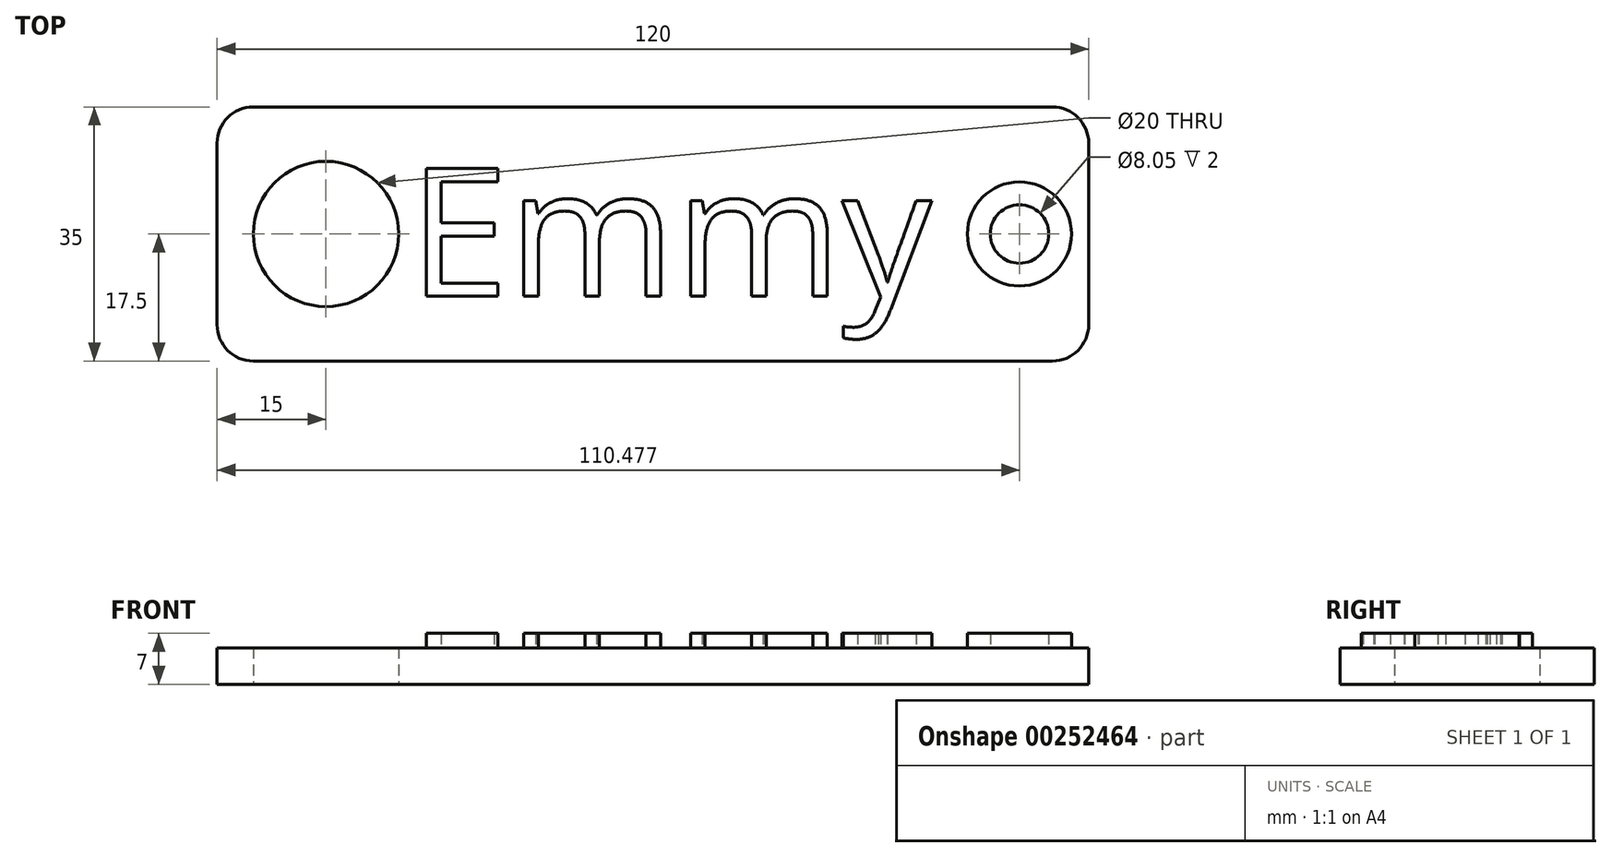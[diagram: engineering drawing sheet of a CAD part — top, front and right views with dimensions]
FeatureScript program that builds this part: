
annotation { "Feature Type Name" : "Feature", "Feature Type Description" : "" }
export const myFeature = defineFeature(function(context is Context, id is Id, definition is map)
    precondition{}
    {
        {
            var Q0;
            Q0=qCreatedBy(makeId("Top.planeOp"),FACE);
            var sketch = newSketch(context, id + "F0", { "sketchPlane" : qUnion([Q0])});
            skLineSegment(sketch, "E0.bottom", {"start": v(60, 17.5) * mm, "end": v(-60, 17.5) * mm});
            skLineSegment(sketch, "E0.top", {"start": v(60, -17.5) * mm, "end": v(-60, -17.5) * mm});
            skLineSegment(sketch, "E0.left", {"start": v(60, 17.5) * mm, "end": v(60, -17.5) * mm});
            skLineSegment(sketch, "E0.right", {"start": v(-60, 17.5) * mm, "end": v(-60, -17.5) * mm});
            skPoint(sketch, "E0.middle", {"position": v(0, 0) * mm});
            skCircle(sketch, "E1", {"center": v(-45, 0) * mm, "radius": 10 * mm});
            skSolve(sketch);
        }
        {
            var Q0;
            Q0=makeQuery(id+"F0.imprint","IMPRINT",FACE,{"disambiguationData":[TD([[makeQuery(id+"F0.imprint","IMPRINT",EDGE,{"derivedFrom":sQuery(id+"F0.wireOp",EDGE,"E0.bottom")}),1.0]])]});
            extrude(context, id + "F1", {"entities" : qUnion([Q0]), "depth" : 5 * mm});
        }
        {
            var Q0;
            Q0=makeQuery(id+"F1.opExtrude","SWEPT_EDGE",EDGE,{"disambiguationData":[OSD([sQuery(id+"F0.wireOp",EDGE,"E0.top"),sQuery(id+"F0.wireOp",EDGE,"E0.right")])]});
            var Q1;
            Q1=makeQuery(id+"F1.opExtrude","SWEPT_EDGE",EDGE,{"disambiguationData":[OSD([sQuery(id+"F0.wireOp",EDGE,"E0.top"),sQuery(id+"F0.wireOp",EDGE,"E0.left")])]});
            var Q2;
            Q2=makeQuery(id+"F1.opExtrude","SWEPT_EDGE",EDGE,{"disambiguationData":[OSD([sQuery(id+"F0.wireOp",EDGE,"E0.bottom"),sQuery(id+"F0.wireOp",EDGE,"E0.left")])]});
            var Q3;
            Q3=makeQuery(id+"F1.opExtrude","SWEPT_EDGE",EDGE,{"disambiguationData":[OSD([sQuery(id+"F0.wireOp",EDGE,"E0.bottom"),sQuery(id+"F0.wireOp",EDGE,"E0.right")])]});
            fillet(context, id + "F2", {"entities" : qUnion([Q0, Q1, Q2, Q3]), "radius" : 5 * mm, "tangentPropagation" : true, "allowEdgeOverflow" : false});
        }
        {
            var Q0;
            Q0=makeQuery(id+"F1.opExtrude","CAP_FACE",FACE,{"disambiguationData":[OSD([sQuery(id+"F0.wireOp",EDGE,"E0.bottom"),sQuery(id+"F0.wireOp",EDGE,"E0.top"),sQuery(id+"F0.wireOp",EDGE,"E0.left"),sQuery(id+"F0.wireOp",EDGE,"E0.right"),sQuery(id+"F0.wireOp",EDGE,"E1")])],"isStart":false});
            var sketch = newSketch(context, id + "F3", { "sketchPlane" : qUnion([Q0])});
            skText(sketch, "E2", { "text": "Emmy", "fontName": "OpenSans-Regular.ttf"});
            skCircle(sketch, "E3", {"center": v(50.48, 0) * mm, "radius": 7.16 * mm});
            skCircle(sketch, "E4", {"center": v(50.48, 0) * mm, "radius": 4.03 * mm});
            const initialGuessF3  = {"E2": [-0.0336, -0.00859, 1, 0, 0.01776]};
            skSetInitialGuess(sketch, initialGuessF3);
            skSolve(sketch);
        }
        {
            var Q0;
            Q0 = qSketchRegion(id + "F3", true);
            extrude(context, id + "F4", {"entities" : qUnion([Q0]), "operationType" : NewBodyOperationType.ADD, "depth" : 2 * mm});
        }
    });
